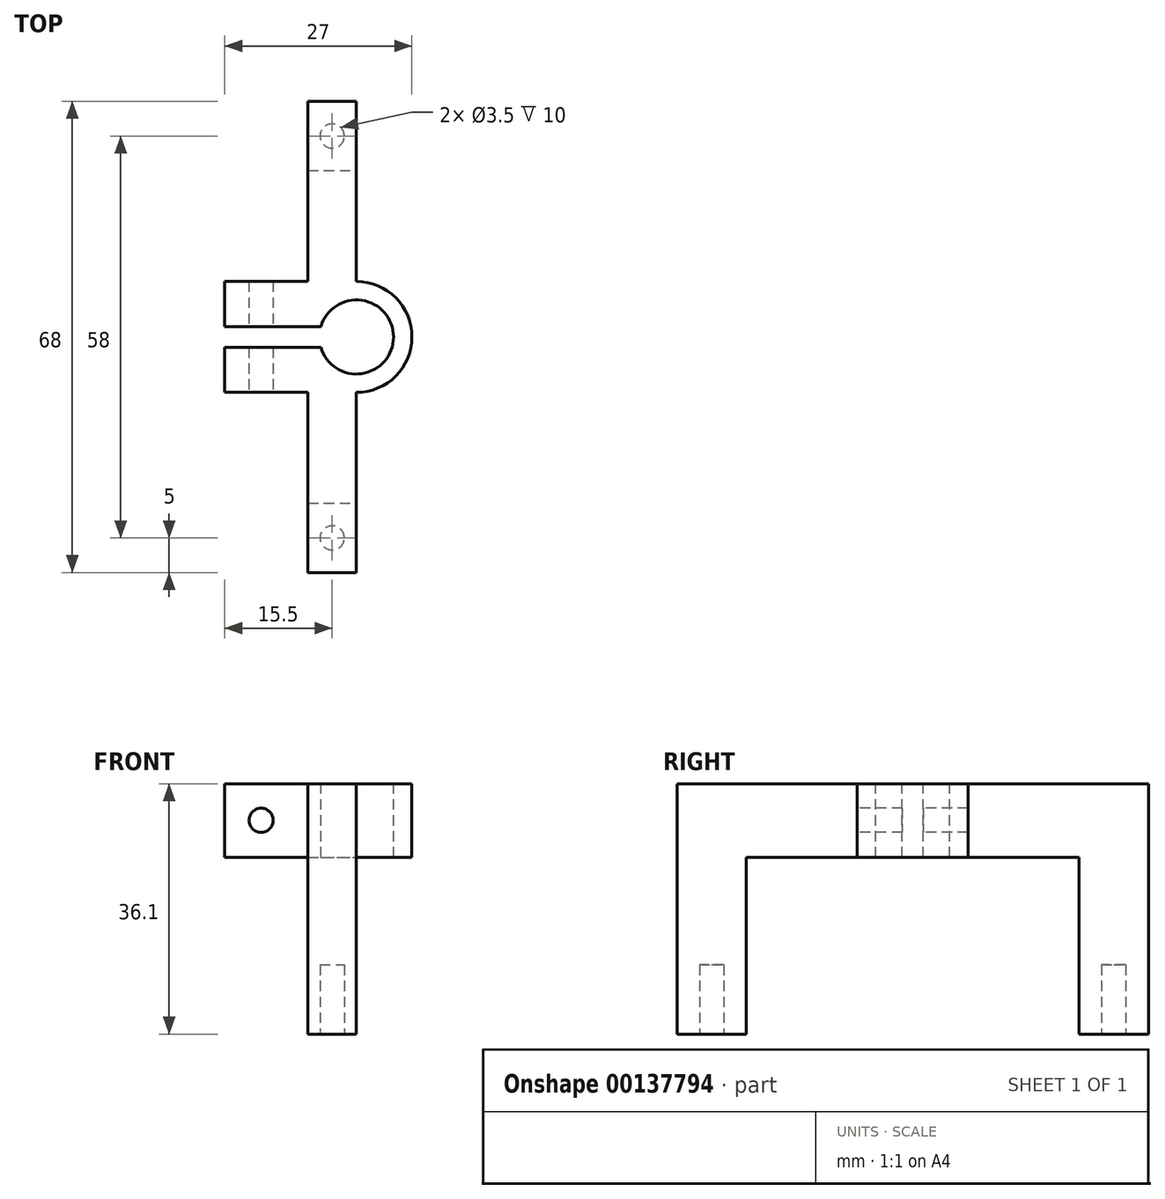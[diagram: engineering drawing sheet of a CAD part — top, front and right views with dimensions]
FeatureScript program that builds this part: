
annotation { "Feature Type Name" : "Feature", "Feature Type Description" : "" }
export const myFeature = defineFeature(function(context is Context, id is Id, definition is map)
    precondition{}
    {
        {
            var Q0;
            Q0=qCreatedBy(makeId("Top.planeOp"),FACE);
            var sketch = newSketch(context, id + "F0", { "sketchPlane" : qUnion([Q0])});
            skCircle(sketch, "E0", {"center": v(0, 0) * mm, "radius": 8 * mm});
            skSolve(sketch);
        }
        {
            var Q0;
            Q0=qSketchRegion(id+"F0",true);
            extrude(context, id + "F1", {"entities" : qUnion([Q0]), "oppositeDirection" : true, "depth" : 10.6 * mm});
        }
        {
            var Q0;
            Q0=makeQuery(id+"F1.opExtrude","CAP_FACE",FACE,{"disambiguationData":[OSD([sQuery(id+"F0.wireOp",EDGE,"E0")])],"isStart":true});
            var sketch = newSketch(context, id + "F2", { "sketchPlane" : qUnion([Q0])});
            skLineSegment(sketch, "E1.bottom", {"start": v(0, 8) * mm, "end": v(-19, 8) * mm});
            skLineSegment(sketch, "E1.top", {"start": v(0, 1.5) * mm, "end": v(-19, 1.5) * mm});
            skLineSegment(sketch, "E1.left", {"start": v(0, 8) * mm, "end": v(0, 1.5) * mm});
            skLineSegment(sketch, "E1.right", {"start": v(-19, 8) * mm, "end": v(-19, 1.5) * mm});
            skLineSegment(sketch, "E2.bottom", {"start": v(0, -8) * mm, "end": v(-19, -8) * mm});
            skLineSegment(sketch, "E2.top", {"start": v(0, -1.5) * mm, "end": v(-19, -1.5) * mm});
            skLineSegment(sketch, "E2.left", {"start": v(0, -8) * mm, "end": v(0, -1.5) * mm});
            skLineSegment(sketch, "E2.right", {"start": v(-19, -8) * mm, "end": v(-19, -1.5) * mm});
            skSolve(sketch);
        }
        {
            var Q0;
            Q0=qSketchRegion(id+"F2",true);
            var Q1;
            Q1=makeQuery(id+"F1.opExtrude","CAP_FACE",FACE,{"disambiguationData":[OSD([sQuery(id+"F0.wireOp",EDGE,"E0")])],"isStart":false});
            extrude(context, id + "F3", {"entities" : qUnion([Q0]), "operationType" : NewBodyOperationType.ADD, "endBound" : BoundingType.UP_TO_SURFACE, "oppositeDirection" : true, "endBoundEntityFace" : qUnion([Q1]), "depth" : 25 * mm});
        }
        {
            var Q0;
            Q0=makeQuery(id+"F3.boolean.opBoolean","MERGE",FACE,{"derivedFrom":[makeQuery(id+"F1.opExtrude","CAP_FACE",FACE,{"disambiguationData":[OSD([sQuery(id+"F0.wireOp",EDGE,"E0")])],"isStart":true}),makeQuery(id+"F3.opExtrude","CAP_FACE",FACE,{"disambiguationData":[OSD([sQuery(id+"F2.wireOp",EDGE,"E1.bottom"),sQuery(id+"F2.wireOp",EDGE,"E1.top"),sQuery(id+"F2.wireOp",EDGE,"E1.left"),sQuery(id+"F2.wireOp",EDGE,"E1.right")])],"isStart":true}),makeQuery(id+"F3.opExtrude","CAP_FACE",FACE,{"disambiguationData":[OSD([sQuery(id+"F2.wireOp",EDGE,"E2.bottom"),sQuery(id+"F2.wireOp",EDGE,"E2.top"),sQuery(id+"F2.wireOp",EDGE,"E2.left"),sQuery(id+"F2.wireOp",EDGE,"E2.right")])],"isStart":true})]});
            var sketch = newSketch(context, id + "F4", { "sketchPlane" : qUnion([Q0])});
            skCircle(sketch, "E3", {"center": v(0, 0) * mm, "radius": 5.35 * mm});
            skSolve(sketch);
        }
        {
            var Q0;
            Q0=qSketchRegion(id+"F4",true);
            extrude(context, id + "F5", {"entities" : qUnion([Q0]), "operationType" : NewBodyOperationType.REMOVE, "endBound" : BoundingType.THROUGH_ALL, "oppositeDirection" : true, "depth" : 25 * mm});
        }
        {
            var Q0;
            Q0=makeQuery(id+"F3.boolean.opBoolean","MERGE",FACE,{"derivedFrom":[makeQuery(id+"F1.opExtrude","CAP_FACE",FACE,{"disambiguationData":[OSD([sQuery(id+"F0.wireOp",EDGE,"E0")])],"isStart":true}),makeQuery(id+"F3.opExtrude","CAP_FACE",FACE,{"disambiguationData":[OSD([sQuery(id+"F2.wireOp",EDGE,"E1.bottom"),sQuery(id+"F2.wireOp",EDGE,"E1.top"),sQuery(id+"F2.wireOp",EDGE,"E1.left"),sQuery(id+"F2.wireOp",EDGE,"E1.right")])],"isStart":true}),makeQuery(id+"F3.opExtrude","CAP_FACE",FACE,{"disambiguationData":[OSD([sQuery(id+"F2.wireOp",EDGE,"E2.bottom"),sQuery(id+"F2.wireOp",EDGE,"E2.top"),sQuery(id+"F2.wireOp",EDGE,"E2.left"),sQuery(id+"F2.wireOp",EDGE,"E2.right")])],"isStart":true})]});
            var sketch = newSketch(context, id + "F6", { "sketchPlane" : qUnion([Q0])});
            skLineSegment(sketch, "E4.bottom", {"start": v(-5.14, -1.5) * mm, "end": v(-10.58, -1.5) * mm});
            skLineSegment(sketch, "E4.top", {"start": v(-5.14, 1.5) * mm, "end": v(-10.58, 1.5) * mm});
            skLineSegment(sketch, "E4.left", {"start": v(-5.14, -1.5) * mm, "end": v(-5.14, 1.5) * mm});
            skLineSegment(sketch, "E4.right", {"start": v(-10.58, -1.5) * mm, "end": v(-10.58, 1.5) * mm});
            skPoint(sketch, "E4.middle", {"position": v(-7.86, 0) * mm});
            skSolve(sketch);
        }
        {
            var Q0;
            Q0=qSketchRegion(id+"F6",true);
            extrude(context, id + "F7", {"entities" : qUnion([Q0]), "operationType" : NewBodyOperationType.REMOVE, "endBound" : BoundingType.THROUGH_ALL, "oppositeDirection" : true, "depth" : 25 * mm});
        }
        {
            var Q0;
            Q0=makeQuery(id+"F3.opExtrude","SWEPT_FACE",FACE,{"disambiguationData":[OSD([sQuery(id+"F2.wireOp",EDGE,"E2.bottom")])]});
            var sketch = newSketch(context, id + "F8", { "sketchPlane" : qUnion([Q0])});
            skCircle(sketch, "E5", {"center": v(-13.75, -5.25) * mm, "radius": 1.75 * mm});
            skSolve(sketch);
        }
        {
            var Q0;
            Q0=qSketchRegion(id+"F8",true);
            extrude(context, id + "F9", {"entities" : qUnion([Q0]), "operationType" : NewBodyOperationType.REMOVE, "endBound" : BoundingType.THROUGH_ALL, "oppositeDirection" : true, "depth" : 25 * mm});
        }
        {
            var Q0;
            Q0=makeQuery(id+"F3.opExtrude","SWEPT_FACE",FACE,{"disambiguationData":[OSD([sQuery(id+"F2.wireOp",EDGE,"E2.bottom")])]});
            var sketch = newSketch(context, id + "F10", { "sketchPlane" : qUnion([Q0])});
            skLineSegment(sketch, "E6.bottom", {"start": v(-7, 0) * mm, "end": v(0, 0) * mm});
            skLineSegment(sketch, "E6.top", {"start": v(-7, -10.6) * mm, "end": v(0, -10.6) * mm});
            skLineSegment(sketch, "E6.left", {"start": v(-7, 0) * mm, "end": v(-7, -10.6) * mm});
            skLineSegment(sketch, "E6.right", {"start": v(0, 0) * mm, "end": v(0, -10.6) * mm});
            skSolve(sketch);
        }
        {
            var Q0;
            Q0=qSketchRegion(id+"F10",true);
            extrude(context, id + "F11", {"entities" : qUnion([Q0]), "operationType" : NewBodyOperationType.ADD, "depth" : 26 * mm});
        }
        {
            var Q0;
            {var subQ0=sQuery(id+"F0.wireOp",EDGE,"E0");Q0=makeQuery(id+"F11.boolean.opBoolean","MERGE",FACE,{"derivedFrom":[makeQuery(id+"F3.boolean.opBoolean","MERGE",FACE,{"derivedFrom":[makeQuery(id+"F1.opExtrude","CAP_FACE",FACE,{"disambiguationData":[OSD([subQ0])],"isStart":false}),makeQuery(id+"F3.opExtrude","CAP_FACE",FACE,{"disambiguationData":[OSD([subQ0]),ownerDisambiguation([makeQuery(id+"F3.opExtrude","SWEPT_BODY",BODY,{"disambiguationData":[OSD([sQuery(id+"F2.wireOp",EDGE,"E1.bottom"),sQuery(id+"F2.wireOp",EDGE,"E1.top"),sQuery(id+"F2.wireOp",EDGE,"E1.left"),sQuery(id+"F2.wireOp",EDGE,"E1.right")])]})])],"isStart":false}),makeQuery(id+"F3.opExtrude","CAP_FACE",FACE,{"disambiguationData":[OSD([subQ0]),ownerDisambiguation([makeQuery(id+"F3.opExtrude","SWEPT_BODY",BODY,{"disambiguationData":[OSD([sQuery(id+"F2.wireOp",EDGE,"E2.bottom"),sQuery(id+"F2.wireOp",EDGE,"E2.top"),sQuery(id+"F2.wireOp",EDGE,"E2.left"),sQuery(id+"F2.wireOp",EDGE,"E2.right")])]})])],"isStart":false})]}),makeQuery(id+"F11.opExtrude","SWEPT_FACE",FACE,{"disambiguationData":[OSD([sQuery(id+"F10.wireOp",EDGE,"E6.top")])]})]});}
            var sketch = newSketch(context, id + "F12", { "sketchPlane" : qUnion([Q0])});
            skLineSegment(sketch, "E7.bottom", {"start": v(-7, 34) * mm, "end": v(0, 34) * mm});
            skLineSegment(sketch, "E7.top", {"start": v(-7, 24) * mm, "end": v(0, 24) * mm});
            skLineSegment(sketch, "E7.left", {"start": v(-7, 34) * mm, "end": v(-7, 24) * mm});
            skLineSegment(sketch, "E7.right", {"start": v(0, 34) * mm, "end": v(0, 24) * mm});
            skSolve(sketch);
        }
        {
            var Q0;
            Q0=qSketchRegion(id+"F12",true);
            extrude(context, id + "F13", {"entities" : qUnion([Q0]), "operationType" : NewBodyOperationType.ADD, "depth" : 25.5 * mm});
        }
        {
            var Q0;
            Q0=makeQuery(id+"F3.opExtrude","SWEPT_FACE",FACE,{"disambiguationData":[OSD([sQuery(id+"F2.wireOp",EDGE,"E1.bottom")])]});
            var sketch = newSketch(context, id + "F14", { "sketchPlane" : qUnion([Q0])});
            skLineSegment(sketch, "E8.bottom", {"start": v(0, 0) * mm, "end": v(7, 0) * mm});
            skLineSegment(sketch, "E8.top", {"start": v(0, -10.6) * mm, "end": v(7, -10.6) * mm});
            skLineSegment(sketch, "E8.left", {"start": v(0, 0) * mm, "end": v(0, -10.6) * mm});
            skLineSegment(sketch, "E8.right", {"start": v(7, 0) * mm, "end": v(7, -10.6) * mm});
            skSolve(sketch);
        }
        {
            var Q0;
            Q0=qSketchRegion(id+"F14",true);
            extrude(context, id + "F15", {"entities" : qUnion([Q0]), "operationType" : NewBodyOperationType.ADD, "depth" : 26 * mm});
        }
        {
            var Q0;
            {var subQ0=sQuery(id+"F0.wireOp",EDGE,"E0");Q0=makeQuery(id+"F15.boolean.opBoolean","MERGE",FACE,{"derivedFrom":[makeQuery(id+"F11.boolean.opBoolean","MERGE",FACE,{"derivedFrom":[makeQuery(id+"F3.boolean.opBoolean","MERGE",FACE,{"derivedFrom":[makeQuery(id+"F1.opExtrude","CAP_FACE",FACE,{"disambiguationData":[OSD([subQ0])],"isStart":false}),makeQuery(id+"F3.opExtrude","CAP_FACE",FACE,{"disambiguationData":[OSD([subQ0]),ownerDisambiguation([makeQuery(id+"F3.opExtrude","SWEPT_BODY",BODY,{"disambiguationData":[OSD([sQuery(id+"F2.wireOp",EDGE,"E1.bottom"),sQuery(id+"F2.wireOp",EDGE,"E1.top"),sQuery(id+"F2.wireOp",EDGE,"E1.left"),sQuery(id+"F2.wireOp",EDGE,"E1.right")])]})])],"isStart":false}),makeQuery(id+"F3.opExtrude","CAP_FACE",FACE,{"disambiguationData":[OSD([subQ0]),ownerDisambiguation([makeQuery(id+"F3.opExtrude","SWEPT_BODY",BODY,{"disambiguationData":[OSD([sQuery(id+"F2.wireOp",EDGE,"E2.bottom"),sQuery(id+"F2.wireOp",EDGE,"E2.top"),sQuery(id+"F2.wireOp",EDGE,"E2.left"),sQuery(id+"F2.wireOp",EDGE,"E2.right")])]})])],"isStart":false})]}),makeQuery(id+"F11.opExtrude","SWEPT_FACE",FACE,{"disambiguationData":[OSD([sQuery(id+"F10.wireOp",EDGE,"E6.top")])]})]}),makeQuery(id+"F15.opExtrude","SWEPT_FACE",FACE,{"disambiguationData":[OSD([sQuery(id+"F14.wireOp",EDGE,"E8.top")])]})]});}
            var sketch = newSketch(context, id + "F16", { "sketchPlane" : qUnion([Q0])});
            skLineSegment(sketch, "E9.bottom", {"start": v(-7, -34) * mm, "end": v(0, -34) * mm});
            skLineSegment(sketch, "E9.top", {"start": v(-7, -24) * mm, "end": v(0, -24) * mm});
            skLineSegment(sketch, "E9.left", {"start": v(-7, -34) * mm, "end": v(-7, -24) * mm});
            skLineSegment(sketch, "E9.right", {"start": v(0, -34) * mm, "end": v(0, -24) * mm});
            skSolve(sketch);
        }
        {
            var Q0;
            Q0=qSketchRegion(id+"F16",true);
            extrude(context, id + "F17", {"entities" : qUnion([Q0]), "operationType" : NewBodyOperationType.ADD, "depth" : 25.5 * mm});
        }
        {
            var Q0;
            Q0=makeQuery(id+"F13.opExtrude","CAP_FACE",FACE,{"disambiguationData":[OSD([sQuery(id+"F12.wireOp",EDGE,"E7.bottom"),sQuery(id+"F12.wireOp",EDGE,"E7.top"),sQuery(id+"F12.wireOp",EDGE,"E7.left"),sQuery(id+"F12.wireOp",EDGE,"E7.right")])],"isStart":false});
            var sketch = newSketch(context, id + "F18", { "sketchPlane" : qUnion([Q0])});
            skCircle(sketch, "E10", {"center": v(-3.5, 29) * mm, "radius": 1.75 * mm});
            skPoint(sketch, "E10.centerSnap0", {"position": v(-7, 29) * mm});
            skLineSegment(sketch, "E11", {"start": v(-3.5, 34) * mm, "end": v(-3.5, 24) * mm, "construction": true});
            skLineSegment(sketch, "E12", {"start": v(-3.5, -24) * mm, "end": v(-3.5, -34) * mm, "construction": true});
            skCircle(sketch, "E13", {"center": v(-3.5, -29) * mm, "radius": 1.75 * mm});
            skSolve(sketch);
        }
        {
            var Q0;
            Q0=qSketchRegion(id+"F18",true);
            extrude(context, id + "F19", {"entities" : qUnion([Q0]), "operationType" : NewBodyOperationType.REMOVE, "oppositeDirection" : true, "depth" : 10 * mm});
        }
    });
